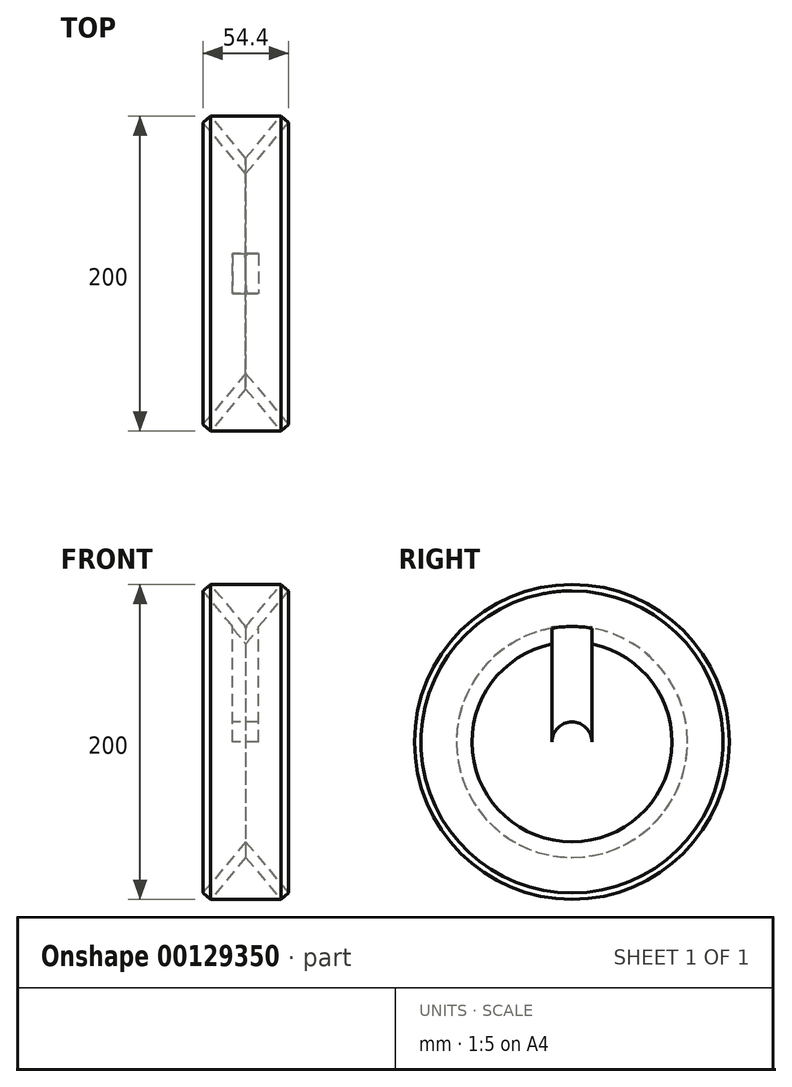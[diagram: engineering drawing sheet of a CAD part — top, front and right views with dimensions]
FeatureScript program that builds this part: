
annotation { "Feature Type Name" : "Feature", "Feature Type Description" : "" }
export const myFeature = defineFeature(function(context is Context, id is Id, definition is map)
    precondition{}
    {
        {
            var Q0;
            Q0=qCreatedBy(makeId("Front.planeOp"),FACE);
            var sketch = newSketch(context, id + "F0", { "sketchPlane" : qUnion([Q0])});
            skLineSegment(sketch, "E0", {"start": v(-22.34, 100) * mm, "end": v(0, 73.38) * mm});
            skLineSegment(sketch, "E1", {"start": v(0, 73.38) * mm, "end": v(22.34, 100) * mm});
            skLineSegment(sketch, "E2", {"start": v(0, 0) * mm, "end": v(0, 100) * mm, "construction": true});
            skLineSegment(sketch, "E3", {"start": v(-108.27, 0) * mm, "end": v(133.77, 0) * mm, "construction": true});
            skLineSegment(sketch, "E4.0", {"start": v(0, 63.5) * mm, "end": v(27.2, 95.92) * mm});
            skLineSegment(sketch, "E4.1", {"start": v(-27.2, 95.92) * mm, "end": v(0, 63.5) * mm});
            skLineSegment(sketch, "E5", {"start": v(-27.2, 95.92) * mm, "end": v(-22.34, 100) * mm});
            skLineSegment(sketch, "E6", {"start": v(22.34, 100) * mm, "end": v(27.2, 95.92) * mm});
            skSolve(sketch);
        }
        {
            var Q0;
            Q0=makeQuery(id+"F0.imprint","IMPRINT",FACE,{"disambiguationData":[TD([[makeQuery(id+"F0.imprint","IMPRINT",EDGE,{"derivedFrom":sQuery(id+"F0.wireOp",EDGE,"E0")}),-1.0]])]});
            var Q1;
            Q1=sQuery(id+"F0.wireOp",EDGE,"E3");
            revolve(context, id + "F1", {"entities" : qUnion([Q0]), "axis" : qUnion([Q1]), "revolveType" : RevolveType.FULL});
        }
        {
            var Q0;
            Q0=qCreatedBy(makeId("Right.planeOp"),FACE);
            var sketch = newSketch(context, id + "F2", { "sketchPlane" : qUnion([Q0])});
            skLineSegment(sketch, "E7.bottom", {"start": v(-12.7, 0) * mm, "end": v(12.7, 0) * mm});
            skLineSegment(sketch, "E7.top", {"start": v(-12.7, 73.38) * mm, "end": v(12.7, 73.38) * mm});
            skLineSegment(sketch, "E7.left", {"start": v(-12.7, 0) * mm, "end": v(-12.7, 73.38) * mm});
            skLineSegment(sketch, "E7.right", {"start": v(12.7, 0) * mm, "end": v(12.7, 73.38) * mm});
            skSolve(sketch);
        }
        {
            var Q0;
            Q0 = qSketchRegion(id + "F2", true);
            var Q1;
            Q1=makeQuery(id+"F1.opRevolve","SWEPT_FACE",FACE,{"disambiguationData":[OSD([sQuery(id+"F0.wireOp",EDGE,"52150f7a-2dcd-47ad-9dc6-daddb4703c43.0")])]});
            extrude(context, id + "F3", {"entities" : qUnion([Q0]), "operationType" : NewBodyOperationType.ADD, "endBound" : BoundingType.SYMMETRIC, "endBoundEntityFace" : qUnion([Q1]), "depth" : 16.5 * mm});
        }
        {
            var Q0;
            {var subQ0=sQuery(id+"F2.wireOp",EDGE,"E7.right");var subQ1=sQuery(id+"F2.wireOp",EDGE,"E7.left");var subQ2=sQuery(id+"F2.wireOp",EDGE,"E7.top");var subQ3=sQuery(id+"F2.wireOp",EDGE,"E7.bottom");Q0=makeQuery(id+"F64PKL8TjYIY3UM_1.2.F3.boolean.opBoolean","MERGE",FACE,{"derivedFrom":[makeQuery(id+"F64PKL8TjYIY3UM_1.1.F3.boolean.opBoolean","MERGE",FACE,{"derivedFrom":[makeQuery(id+"F3.opExtrude","CAP_FACE",FACE,{"disambiguationData":[OSD([subQ3,subQ2,subQ1,subQ0])],"isStart":true}),makeQuery(id+"F64PKL8TjYIY3UM_1.1.F3.opExtrude","CAP_FACE",FACE,{"disambiguationData":[OSD([subQ3,subQ2,subQ1,subQ0])],"isStart":true})]}),makeQuery(id+"F64PKL8TjYIY3UM_1.2.F3.opExtrude","CAP_FACE",FACE,{"disambiguationData":[OSD([subQ3,subQ2,subQ1,subQ0])],"isStart":true})]});}
            var sketch = newSketch(context, id + "F4", { "sketchPlane" : qUnion([Q0])});
            skCircle(sketch, "E8", {"center": v(0, 0) * mm, "radius": 12.7 * mm});
            skSolve(sketch);
        }
        {
            var Q0;
            Q0 = qSketchRegion(id + "F4", true);
            extrude(context, id + "F5", {"entities" : qUnion([Q0]), "operationType" : NewBodyOperationType.REMOVE, "endBound" : BoundingType.THROUGH_ALL, "oppositeDirection" : true, "depth" : 25.4 * mm});
        }
        {
            var Q0;
            Q0=qCreatedBy(makeId("Front.planeOp"),FACE);
            var sketch = newSketch(context, id + "F6", { "sketchPlane" : qUnion([Q0])});
            skLineSegment(sketch, "E9", {"start": v(-93.5, 0) * mm, "end": v(102.53, 0) * mm, "construction": true});
            skLineSegment(sketch, "E10", {"start": v(-22.34, 100) * mm, "end": v(0, 73.38) * mm});
            skLineSegment(sketch, "E11", {"start": v(0, 73.38) * mm, "end": v(22.34, 100) * mm});
            skLineSegment(sketch, "E12", {"start": v(-22.34, 100) * mm, "end": v(22.34, 100) * mm});
            skSolve(sketch);
        }
        {
            var Q0;
            Q0=makeQuery(id+"F6.imprint","IMPRINT",FACE,{"disambiguationData":[TD([[makeQuery(id+"F6.imprint","IMPRINT",EDGE,{"derivedFrom":sQuery(id+"F6.wireOp",EDGE,"E10")}),1.0]])]});
            var Q1;
            Q1=sQuery(id+"F6.wireOp",EDGE,"E9");
            revolve(context, id + "F7", {"entities" : qUnion([Q0]), "axis" : qUnion([Q1]), "revolveType" : RevolveType.FULL});
        }
    });
